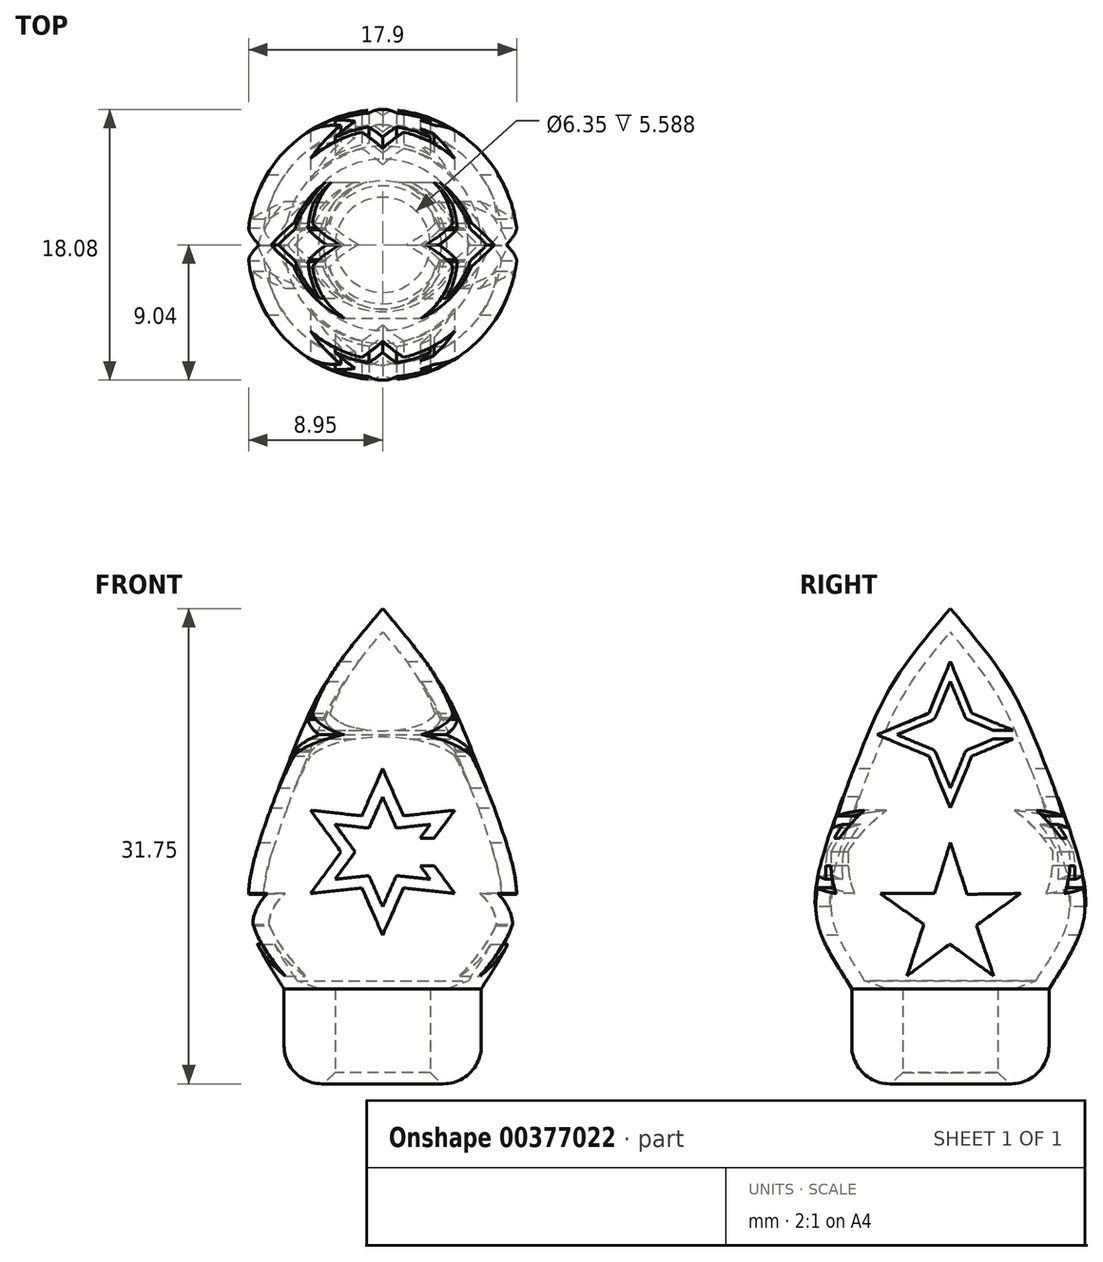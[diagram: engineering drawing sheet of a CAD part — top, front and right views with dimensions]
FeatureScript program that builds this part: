
annotation { "Feature Type Name" : "Feature", "Feature Type Description" : "" }
export const myFeature = defineFeature(function(context is Context, id is Id, definition is map)
    precondition{}
    {
        {
            var Q0;
            Q0=qCreatedBy(makeId("Top.planeOp"),FACE);
            var sketch = newSketch(context, id + "F0", { "sketchPlane" : qUnion([Q0])});
            skCircle(sketch, "E0", {"center": v(0, 0) * mm, "radius": 3.18 * mm});
            skCircle(sketch, "E1", {"center": v(0, 0) * mm, "radius": 6.59 * mm});
            skSolve(sketch);
        }
        {
            var Q0;
            Q0 = qSketchRegion(id + "F0", true);
            extrude(context, id + "F1", {"entities" : qUnion([Q0]), "depth" : 25.4 * mm});
        }
        {
            var Q0;
            Q0=makeQuery(id+"F1.opExtrude","SWEPT_BODY",BODY,{"disambiguationData":[OSD([sQuery(id+"F0.wireOp",EDGE,"E0"),sQuery(id+"F0.wireOp",EDGE,"E1")])]});
            deleteBodies(context, id + "F2", {"entities" : qUnion([Q0])});
        }
        {
            var Q0;
            Q0 = qSketchRegion(id + "F0", true);
            extrude(context, id + "F3", {"entities" : qUnion([Q0]), "depth" : 6.35 * mm});
        }
        {
            var Q0;
            Q0=makeQuery(id+"F3.opExtrude","CAP_FACE",FACE,{"disambiguationData":[OSD([sQuery(id+"F0.wireOp",EDGE,"E0"),sQuery(id+"F0.wireOp",EDGE,"E1")])],"isStart":false});
            var sketch = newSketch(context, id + "F4", { "sketchPlane" : qUnion([Q0])});
            skLineSegment(sketch, "E2", {"start": v(0, 0) * mm, "end": v(6.59, 0) * mm});
            skSolve(sketch);
        }
        {
            var Q0;
            Q0=qCreatedBy(makeId("Front.planeOp"),FACE);
            var sketch = newSketch(context, id + "F5", { "sketchPlane" : qUnion([Q0])});
            skLineSegment(sketch, "E3", {"start": v(0, 6.35) * mm, "end": v(0, 31.75) * mm});
            skFitSpline(sketch, "E4", {"points": [v(0, 31.75) * mm, v(3.77, 26.85) * mm, v(6.01, 22.12) * mm, v(8.38, 15.68) * mm, v(8.87, 10.75) * mm, v(6.59, 6.35) * mm], "startDerivative": vector(19.48, -23.04) * mm, "endDerivative": vector(-12.94, -20.96) * mm});
            skFitSpline(sketch, "E5.0", {"points": [v(-0.78, 31.1) * mm, v(-0.37, 30.61) * mm, v(0.44, 29.65) * mm, v(1.6, 28.22) * mm, v(2.45, 27.04) * mm, v(3.03, 26.12) * mm, v(3.56, 25.2) * mm, v(4.13, 24.03) * mm, v(4.66, 22.77) * mm, v(5.1, 21.66) * mm, v(5.57, 20.5) * mm, v(6.16, 18.98) * mm, v(6.73, 17.44) * mm, v(7.14, 16.23) * mm, v(7.42, 15.35) * mm, v(7.67, 14.52) * mm, v(7.85, 13.73) * mm, v(7.98, 12.98) * mm, v(8.03, 12.28) * mm, v(8.01, 11.73) * mm, v(7.95, 11.3) * mm, v(7.89, 10.98) * mm, v(7.8, 10.66) * mm, v(7.64, 10.22) * mm, v(7.39, 9.65) * mm, v(7.01, 8.96) * mm, v(6.45, 8.03) * mm, v(6, 7.34) * mm, v(5.72, 6.88) * mm]});
            skLineSegment(sketch, "E6", {"start": v(5.72, 6.88) * mm, "end": v(4.28, 6.35) * mm});
            skLineSegment(sketch, "E7", {"start": v(4.28, 6.35) * mm, "end": v(6.59, 6.35) * mm});
            skSolve(sketch);
        }
        {
            var Q0;
            {var subQ1=sQuery(id+"F5.wireOp",EDGE,"E4");Q0=makeQuery(id+"F5.imprint","IMPRINT",FACE,{"disambiguationData":[TD([[makeQuery(id+"F5.imprint","IMPRINT",EDGE,{"derivedFrom":subQ1}),-1.0]])]});}
            var Q1;
            Q1=sQuery(id+"F5.wireOp",EDGE,"E3");
            revolve(context, id + "F6", {"operationType" : NewBodyOperationType.ADD, "entities" : qUnion([Q0]), "axis" : qUnion([Q1]), "revolveType" : RevolveType.FULL});
        }
        {
            var Q0;
            Q0=qCreatedBy(makeId("Front.planeOp"),FACE);
            var sketch = newSketch(context, id + "F7", { "sketchPlane" : qUnion([Q0])});
            skLineSegment(sketch, "E8", {"start": v(0, 15.5) * mm, "end": v(0, 18.27) * mm});
            skLineSegment(sketch, "E9", {"start": v(0, 15.5) * mm, "end": v(2.78, 20.3) * mm});
            skLineSegment(sketch, "E10", {"start": v(0, 21.05) * mm, "end": v(1.39, 17.9) * mm});
            skPoint(sketch, "E10.endSnap0", {"position": v(1.39, 17.9) * mm});
            skLineSegment(sketch, "E11.MirrorCS", {"start": v(0, 21.05) * mm, "end": v(-1.39, 17.9) * mm});
            skLineSegment(sketch, "E12.1.0", {"start": v(-4.81, 18.27) * mm, "end": v(-1.39, 17.9) * mm});
            skLineSegment(sketch, "E12.1.1", {"start": v(-4.81, 18.27) * mm, "end": v(-2.78, 15.5) * mm});
            skLineSegment(sketch, "E12.2.0", {"start": v(-4.81, 12.71) * mm, "end": v(-2.78, 15.5) * mm});
            skLineSegment(sketch, "E12.2.1", {"start": v(-4.81, 12.71) * mm, "end": v(-1.39, 13.09) * mm});
            skLineSegment(sketch, "E12.3.0", {"start": v(0, 9.94) * mm, "end": v(-1.39, 13.09) * mm});
            skLineSegment(sketch, "E12.3.1", {"start": v(0, 9.94) * mm, "end": v(1.39, 13.09) * mm});
            skLineSegment(sketch, "E12.4.0", {"start": v(4.81, 12.71) * mm, "end": v(1.39, 13.09) * mm});
            skLineSegment(sketch, "E12.4.1", {"start": v(4.81, 12.71) * mm, "end": v(3.45, 14.58) * mm});
            skLineSegment(sketch, "E12.5.0", {"start": v(4.81, 18.27) * mm, "end": v(3.45, 16.4) * mm});
            skLineSegment(sketch, "E12.5.1", {"start": v(4.81, 18.27) * mm, "end": v(1.39, 17.9) * mm});
            skPoint(sketch, "E12.center", {"position": v(0, 15.5) * mm});
            skLineSegment(sketch, "E13.0", {"start": v(-3.18, 17.33) * mm, "end": v(-1.83, 15.5) * mm});
            skLineSegment(sketch, "E13.1", {"start": v(3.18, 17.33) * mm, "end": v(2.5, 16.4) * mm});
            skLineSegment(sketch, "E13.2", {"start": v(3.18, 17.33) * mm, "end": v(0.92, 17.08) * mm});
            skLineSegment(sketch, "E13.3", {"start": v(0, 19.16) * mm, "end": v(0.92, 17.08) * mm});
            skLineSegment(sketch, "E13.4", {"start": v(0, 19.16) * mm, "end": v(-0.92, 17.08) * mm});
            skLineSegment(sketch, "E13.5", {"start": v(3.18, 13.66) * mm, "end": v(2.5, 14.58) * mm});
            skLineSegment(sketch, "E13.6", {"start": v(-3.18, 17.33) * mm, "end": v(-0.92, 17.08) * mm});
            skLineSegment(sketch, "E13.7", {"start": v(3.18, 13.66) * mm, "end": v(0.92, 13.9) * mm});
            skLineSegment(sketch, "E13.8", {"start": v(0, 11.82) * mm, "end": v(0.92, 13.9) * mm});
            skLineSegment(sketch, "E13.9", {"start": v(0, 11.82) * mm, "end": v(-0.92, 13.9) * mm});
            skLineSegment(sketch, "E13.10", {"start": v(-3.18, 13.66) * mm, "end": v(-0.92, 13.9) * mm});
            skLineSegment(sketch, "E13.11", {"start": v(-3.18, 13.66) * mm, "end": v(-1.83, 15.5) * mm});
            skLineSegment(sketch, "E14", {"start": v(0, 15.5) * mm, "end": v(1.83, 15.5) * mm});
            skPoint(sketch, "E15.endSnap0", {"position": v(2.5, 16.4) * mm});
            skLineSegment(sketch, "E16", {"start": v(2.5, 16.4) * mm, "end": v(3.45, 16.4) * mm});
            skLineSegment(sketch, "E17", {"start": v(1.83, 15.5) * mm, "end": v(2.78, 15.5) * mm});
            skLineSegment(sketch, "E18.MirrorCS", {"start": v(2.5, 14.58) * mm, "end": v(3.45, 14.58) * mm});
            skPoint(sketch, "E19.orphan", {"position": v(1.83, 14.58) * mm});
            skPoint(sketch, "E20.orphan", {"position": v(1.83, 16.4) * mm});
            skPoint(sketch, "E21.orphan", {"position": v(2.78, 15.5) * mm});
            skSolve(sketch);
        }
        {
            var Q0;
            Q0 = qSketchRegion(id + "F7", true);
            extrude(context, id + "F8", {"entities" : qUnion([Q0]), "operationType" : NewBodyOperationType.REMOVE, "endBound" : BoundingType.SYMMETRIC, "oppositeDirection" : true, "depth" : 127 * mm});
        }
        {
            var Q0;
            Q0=qCreatedBy(makeId("Right.planeOp"),FACE);
            var sketch = newSketch(context, id + "F9", { "sketchPlane" : qUnion([Q0])});
            skArc(sketch, "E22", {"start": v(1.12, 12.65) * mm, "mid": v(1.12, 12.66) * mm, "end": v(1.11, 12.66) * mm});
            skLineSegment(sketch, "E23", {"start": v(0, 11.19) * mm, "end": v(0, 16.11) * mm});
            skLineSegment(sketch, "E24", {"start": v(0, 16.11) * mm, "end": v(-1.06, 12.7) * mm});
            skLineSegment(sketch, "E25", {"start": v(-1.06, 12.7) * mm, "end": v(0, 16.11) * mm});
            skLineSegment(sketch, "E26", {"start": v(1.12, 12.65) * mm, "end": v(0, 16.11) * mm});
            skLineSegment(sketch, "E27.1.0", {"start": v(-1.77, 10.65) * mm, "end": v(-4.69, 12.71) * mm});
            skLineSegment(sketch, "E27.1.1", {"start": v(-1.05, 12.71) * mm, "end": v(-4.69, 12.71) * mm});
            skLineSegment(sketch, "E27.2.0", {"start": v(-0.04, 9.34) * mm, "end": v(-2.9, 7.2) * mm});
            skLineSegment(sketch, "E27.2.1", {"start": v(-1.77, 10.66) * mm, "end": v(-2.9, 7.2) * mm});
            skLineSegment(sketch, "E27.3.0", {"start": v(1.75, 10.58) * mm, "end": v(2.9, 7.2) * mm});
            skLineSegment(sketch, "E27.3.1", {"start": v(-0.05, 9.34) * mm, "end": v(2.9, 7.2) * mm});
            skLineSegment(sketch, "E27.4.0", {"start": v(1.11, 12.66) * mm, "end": v(4.69, 12.71) * mm});
            skLineSegment(sketch, "E27.4.1", {"start": v(1.74, 10.57) * mm, "end": v(4.69, 12.71) * mm});
            skArc(sketch, "E28.trimOffspring", {"start": v(-1.05, 12.71) * mm, "mid": v(-1.05, 12.7) * mm, "end": v(-1.06, 12.7) * mm});
            skArc(sketch, "E29.trimOffspring", {"start": v(1.74, 10.57) * mm, "mid": v(1.74, 10.58) * mm, "end": v(1.75, 10.58) * mm});
            skArc(sketch, "E30.trimOffspring", {"start": v(-0.05, 9.34) * mm, "mid": v(-0.04, 9.34) * mm, "end": v(-0.04, 9.34) * mm});
            skArc(sketch, "E31.trimOffspring", {"start": v(-1.77, 10.66) * mm, "mid": v(-1.77, 10.66) * mm, "end": v(-1.77, 10.65) * mm});
            skArc(sketch, "E32", {"start": v(1.14, 24.33) * mm, "mid": v(1.07, 24.4) * mm, "end": v(1, 24.45) * mm});
            skLineSegment(sketch, "E33", {"start": v(0, 23.32) * mm, "end": v(0, 26.88) * mm});
            skLineSegment(sketch, "E34", {"start": v(0, 26.88) * mm, "end": v(1, 24.45) * mm});
            skLineSegment(sketch, "E35.MirrorCS", {"start": v(0, 26.88) * mm, "end": v(-1, 24.45) * mm});
            skLineSegment(sketch, "E36.1.0", {"start": v(-3.57, 23.32) * mm, "end": v(-1.14, 22.31) * mm});
            skLineSegment(sketch, "E36.1.1", {"start": v(-3.57, 23.32) * mm, "end": v(-1.14, 24.33) * mm});
            skLineSegment(sketch, "E36.2.0", {"start": v(0, 19.75) * mm, "end": v(1, 22.18) * mm});
            skLineSegment(sketch, "E36.2.1", {"start": v(0, 19.75) * mm, "end": v(-1, 22.18) * mm});
            skLineSegment(sketch, "E36.3.0", {"start": v(2.86, 23.61) * mm, "end": v(1.14, 24.33) * mm});
            skLineSegment(sketch, "E36.3.1", {"start": v(2.86, 23.03) * mm, "end": v(1.14, 22.31) * mm});
            skArc(sketch, "E37.trimOffspring", {"start": v(-1, 24.45) * mm, "mid": v(-1.07, 24.4) * mm, "end": v(-1.14, 24.33) * mm});
            skArc(sketch, "E38.trimOffspring", {"start": v(-1.14, 22.31) * mm, "mid": v(-1.07, 22.25) * mm, "end": v(-1, 22.18) * mm});
            skArc(sketch, "E39.trimOffspring", {"start": v(1, 22.18) * mm, "mid": v(1.07, 22.25) * mm, "end": v(1.14, 22.31) * mm});
            skLineSegment(sketch, "E40.0", {"start": v(4.19, 23.03) * mm, "end": v(1.43, 21.89) * mm});
            skLineSegment(sketch, "E40.1", {"start": v(0, 18.42) * mm, "end": v(1.43, 21.89) * mm});
            skLineSegment(sketch, "E40.2", {"start": v(4.19, 23.61) * mm, "end": v(1.43, 24.75) * mm});
            skLineSegment(sketch, "E40.3", {"start": v(0, 18.42) * mm, "end": v(-1.43, 21.89) * mm});
            skLineSegment(sketch, "E40.4", {"start": v(0, 28.21) * mm, "end": v(1.43, 24.75) * mm});
            skLineSegment(sketch, "E40.5", {"start": v(0, 28.21) * mm, "end": v(-1.43, 24.75) * mm});
            skLineSegment(sketch, "E40.6", {"start": v(-4.9, 23.32) * mm, "end": v(-1.43, 24.75) * mm});
            skLineSegment(sketch, "E40.7", {"start": v(-4.9, 23.32) * mm, "end": v(-1.43, 21.89) * mm});
            skLineSegment(sketch, "E41", {"start": v(2.86, 23.61) * mm, "end": v(4.19, 23.61) * mm});
            skLineSegment(sketch, "E42.MirrorCS", {"start": v(2.86, 23.03) * mm, "end": v(4.19, 23.03) * mm});
            skPoint(sketch, "E43.orphan", {"position": v(3.57, 23.32) * mm});
            skSolve(sketch);
        }
        {
            var Q0;
            Q0 = qSketchRegion(id + "F9", true);
            extrude(context, id + "F10", {"entities" : qUnion([Q0]), "operationType" : NewBodyOperationType.REMOVE, "endBound" : BoundingType.SYMMETRIC, "oppositeDirection" : true, "depth" : 127 * mm});
        }
        {
            var Q0;
            Q0=makeQuery(id+"F3.opExtrude","CAP_EDGE",EDGE,{"disambiguationData":[OSD([sQuery(id+"F0.wireOp",EDGE,"E1")])],"isStart":true});
            fillet(context, id + "F11", {"entities" : qUnion([Q0]), "radius" : 2.54 * mm, "tangentPropagation" : true, "allowEdgeOverflow" : false});
        }
        {
            var Q0;
            Q0=makeQuery(id+"F3.opExtrude","CAP_EDGE",EDGE,{"disambiguationData":[OSD([sQuery(id+"F0.wireOp",EDGE,"E0")])],"isStart":true});
            chamfer(context, id + "F12", {"entities" : qUnion([Q0]), "width" : 0.76 * mm, "tangentPropagation" : true});
        }
    });
